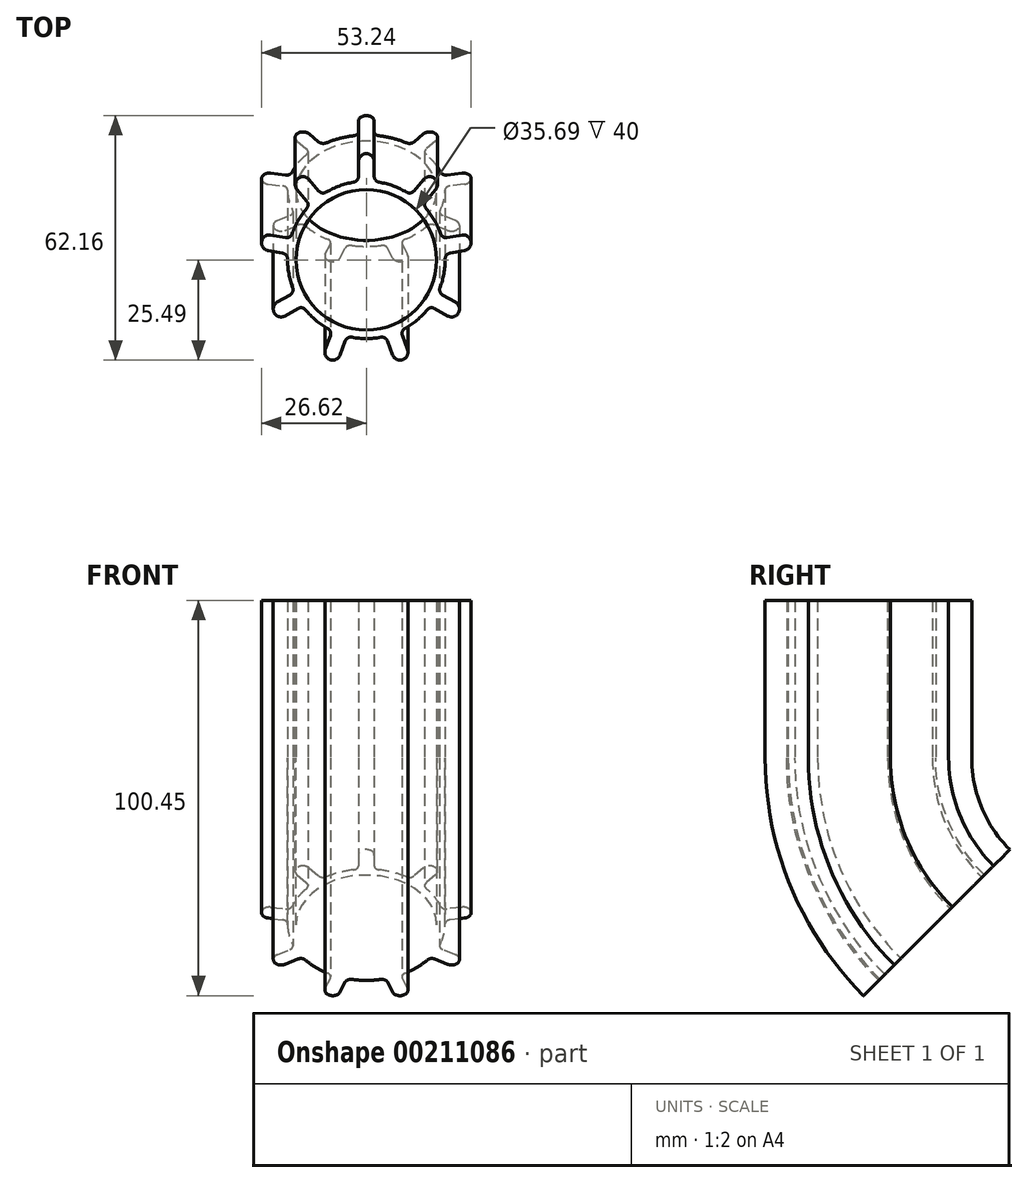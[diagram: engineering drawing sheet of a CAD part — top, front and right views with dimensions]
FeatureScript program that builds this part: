
annotation { "Feature Type Name" : "Feature", "Feature Type Description" : "" }
export const myFeature = defineFeature(function(context is Context, id is Id, definition is map)
    precondition{}
    {
        {
            var Q0;
            Q0=qCreatedBy(makeId("Top.planeOp"),FACE);
            var sketch = newSketch(context, id + "F0", { "sketchPlane" : qUnion([Q0])});
            skArc(sketch, "E0", {"start": v(-3.26, 19.73) * mm, "mid": v(-6.84, 18.8) * mm, "end": v(-10.2, 17.2) * mm});
            skArc(sketch, "E1", {"start": v(2, 25) * mm, "mid": v(0, 27) * mm, "end": v(-2, 25) * mm});
            skLineSegment(sketch, "E2", {"start": v(-2, 25) * mm, "end": v(-2, 21.21) * mm});
            skLineSegment(sketch, "E3", {"start": v(2, 25) * mm, "end": v(2, 21.21) * mm});
            skPoint(sketch, "E4.visualSharp", {"position": v(-2, 19.9) * mm});
            skArc(sketch, "E4.filletArc", {"start": v(-3.26, 19.73) * mm, "mid": v(-2.36, 20.24) * mm, "end": v(-2, 21.21) * mm});
            skPoint(sketch, "E5.visualSharp", {"position": v(2, 19.9) * mm});
            skArc(sketch, "E5.filletArc", {"start": v(2, 21.21) * mm, "mid": v(2.36, 20.24) * mm, "end": v(3.26, 19.73) * mm});
            skArc(sketch, "E6.1.0", {"start": v(-15.18, 13.02) * mm, "mid": v(-14.82, 14) * mm, "end": v(-15.17, 14.96) * mm});
            skLineSegment(sketch, "E6.1.1", {"start": v(-17.6, 17.87) * mm, "end": v(-15.17, 14.96) * mm});
            skArc(sketch, "E6.1.2", {"start": v(-14.54, 20.44) * mm, "mid": v(-17.36, 20.68) * mm, "end": v(-17.6, 17.87) * mm});
            skLineSegment(sketch, "E6.1.3", {"start": v(-14.54, 20.44) * mm, "end": v(-12.1, 17.54) * mm});
            skArc(sketch, "E6.1.4", {"start": v(-12.1, 17.54) * mm, "mid": v(-11.2, 17.02) * mm, "end": v(-10.2, 17.2) * mm});
            skArc(sketch, "E6.2.0", {"start": v(-20, 0.22) * mm, "mid": v(-20.34, 1.2) * mm, "end": v(-21.24, 1.71) * mm});
            skLineSegment(sketch, "E6.2.1", {"start": v(-24.97, 2.37) * mm, "end": v(-21.24, 1.71) * mm});
            skArc(sketch, "E6.2.2", {"start": v(-24.27, 6.31) * mm, "mid": v(-26.59, 4.69) * mm, "end": v(-24.97, 2.37) * mm});
            skLineSegment(sketch, "E6.2.3", {"start": v(-24.27, 6.31) * mm, "end": v(-20.54, 5.65) * mm});
            skArc(sketch, "E6.2.4", {"start": v(-20.54, 5.65) * mm, "mid": v(-19.53, 5.84) * mm, "end": v(-18.87, 6.63) * mm});
            skArc(sketch, "E6.3.0", {"start": v(-15.46, -12.69) * mm, "mid": v(-16.35, -12.16) * mm, "end": v(-17.37, -12.34) * mm});
            skLineSegment(sketch, "E6.3.1", {"start": v(-20.65, -14.23) * mm, "end": v(-17.37, -12.34) * mm});
            skArc(sketch, "E6.3.2", {"start": v(-22.65, -10.77) * mm, "mid": v(-23.38, -13.5) * mm, "end": v(-20.65, -14.23) * mm});
            skLineSegment(sketch, "E6.3.3", {"start": v(-22.65, -10.77) * mm, "end": v(-19.37, -8.87) * mm});
            skArc(sketch, "E6.3.4", {"start": v(-19.37, -8.87) * mm, "mid": v(-18.7, -8.08) * mm, "end": v(-18.72, -7.05) * mm});
            skArc(sketch, "E6.4.0", {"start": v(-3.69, -19.66) * mm, "mid": v(-4.7, -19.83) * mm, "end": v(-5.38, -20.62) * mm});
            skLineSegment(sketch, "E6.4.1", {"start": v(-6.67, -24.18) * mm, "end": v(-5.38, -20.62) * mm});
            skArc(sketch, "E6.4.2", {"start": v(-10.43, -22.8) * mm, "mid": v(-9.23, -25.37) * mm, "end": v(-6.67, -24.18) * mm});
            skLineSegment(sketch, "E6.4.3", {"start": v(-10.43, -22.8) * mm, "end": v(-9.13, -19.25) * mm});
            skArc(sketch, "E6.4.4", {"start": v(-9.13, -19.25) * mm, "mid": v(-9.14, -18.22) * mm, "end": v(-9.8, -17.43) * mm});
            skArc(sketch, "E6.5.0", {"start": v(9.8, -17.43) * mm, "mid": v(9.14, -18.22) * mm, "end": v(9.13, -19.25) * mm});
            skLineSegment(sketch, "E6.5.1", {"start": v(10.43, -22.8) * mm, "end": v(9.13, -19.25) * mm});
            skArc(sketch, "E6.5.2", {"start": v(6.67, -24.18) * mm, "mid": v(9.23, -25.37) * mm, "end": v(10.43, -22.8) * mm});
            skLineSegment(sketch, "E6.5.3", {"start": v(6.67, -24.18) * mm, "end": v(5.38, -20.62) * mm});
            skArc(sketch, "E6.5.4", {"start": v(5.38, -20.62) * mm, "mid": v(4.7, -19.83) * mm, "end": v(3.69, -19.66) * mm});
            skArc(sketch, "E6.6.0", {"start": v(18.72, -7.05) * mm, "mid": v(18.7, -8.08) * mm, "end": v(19.37, -8.87) * mm});
            skLineSegment(sketch, "E6.6.1", {"start": v(22.65, -10.77) * mm, "end": v(19.37, -8.87) * mm});
            skArc(sketch, "E6.6.2", {"start": v(20.65, -14.23) * mm, "mid": v(23.38, -13.5) * mm, "end": v(22.65, -10.77) * mm});
            skLineSegment(sketch, "E6.6.3", {"start": v(20.65, -14.23) * mm, "end": v(17.37, -12.34) * mm});
            skArc(sketch, "E6.6.4", {"start": v(17.37, -12.34) * mm, "mid": v(16.35, -12.16) * mm, "end": v(15.46, -12.69) * mm});
            skArc(sketch, "E6.7.0", {"start": v(18.87, 6.63) * mm, "mid": v(19.53, 5.84) * mm, "end": v(20.54, 5.65) * mm});
            skLineSegment(sketch, "E6.7.1", {"start": v(24.27, 6.31) * mm, "end": v(20.54, 5.65) * mm});
            skArc(sketch, "E6.7.2", {"start": v(24.97, 2.37) * mm, "mid": v(26.59, 4.69) * mm, "end": v(24.27, 6.31) * mm});
            skLineSegment(sketch, "E6.7.3", {"start": v(24.97, 2.37) * mm, "end": v(21.24, 1.71) * mm});
            skArc(sketch, "E6.7.4", {"start": v(21.24, 1.71) * mm, "mid": v(20.34, 1.2) * mm, "end": v(20, 0.22) * mm});
            skArc(sketch, "E6.8.0", {"start": v(10.2, 17.2) * mm, "mid": v(11.2, 17.02) * mm, "end": v(12.1, 17.54) * mm});
            skLineSegment(sketch, "E6.8.1", {"start": v(14.54, 20.44) * mm, "end": v(12.1, 17.54) * mm});
            skArc(sketch, "E6.8.2", {"start": v(17.6, 17.87) * mm, "mid": v(17.36, 20.68) * mm, "end": v(14.54, 20.44) * mm});
            skLineSegment(sketch, "E6.8.3", {"start": v(17.6, 17.87) * mm, "end": v(15.17, 14.96) * mm});
            skArc(sketch, "E6.8.4", {"start": v(15.17, 14.96) * mm, "mid": v(14.82, 14) * mm, "end": v(15.18, 13.02) * mm});
            skArc(sketch, "E7.trimOffspring", {"start": v(-20, 0.22) * mm, "mid": v(-19.7, -3.47) * mm, "end": v(-18.72, -7.05) * mm});
            skArc(sketch, "E8.trimOffspring", {"start": v(-15.18, 13.02) * mm, "mid": v(-17.32, 10) * mm, "end": v(-18.87, 6.63) * mm});
            skArc(sketch, "E9.trimOffspring", {"start": v(10.2, 17.2) * mm, "mid": v(6.84, 18.8) * mm, "end": v(3.26, 19.73) * mm});
            skPoint(sketch, "E10.center.orphan", {"position": v(0, -25) * mm});
            skArc(sketch, "E11.trimOffspring", {"start": v(-3.69, -19.66) * mm, "mid": v(0, -20) * mm, "end": v(3.69, -19.66) * mm});
            skArc(sketch, "E12.trimOffspring", {"start": v(-15.46, -12.69) * mm, "mid": v(-12.86, -15.32) * mm, "end": v(-9.8, -17.43) * mm});
            skArc(sketch, "E13.trimOffspring", {"start": v(9.8, -17.43) * mm, "mid": v(12.86, -15.32) * mm, "end": v(15.46, -12.69) * mm});
            skArc(sketch, "E14.trimOffspring", {"start": v(18.72, -7.05) * mm, "mid": v(19.7, -3.47) * mm, "end": v(20, 0.22) * mm});
            skArc(sketch, "E15.trimOffspring", {"start": v(18.87, 6.63) * mm, "mid": v(17.32, 10) * mm, "end": v(15.18, 13.02) * mm});
            skCircle(sketch, "E16", {"center": v(0, 0) * mm, "radius": 17.84 * mm});
            skSolve(sketch);
        }
        {
            var Q0;
            Q0=qCreatedBy(makeId("Right.planeOp"),FACE);
            var sketch = newSketch(context, id + "F1", { "sketchPlane" : qUnion([Q0])});
            skLineSegment(sketch, "E17", {"start": v(0, 0) * mm, "end": v(0, -40) * mm});
            skPoint(sketch, "E18.visualSharp", {"position": v(0, -100) * mm});
            skArc(sketch, "E18.filletArc", {"start": v(0, -40) * mm, "mid": v(4.57, -62.96) * mm, "end": v(17.57, -82.43) * mm});
            skLineSegment(sketch, "E19", {"start": v(0, -100) * mm, "end": v(17.57, -82.43) * mm});
            skLineSegment(sketch, "E20", {"start": v(0, -100) * mm, "end": v(0, -40) * mm, "construction": true});
            skPoint(sketch, "E21.end.orphan", {"position": v(100, -100) * mm});
            skSolve(sketch);
        }
        {
            var Q0;
            Q0=makeQuery(id+"F0.imprint","IMPRINT",FACE,{"disambiguationData":[TD([[makeQuery(id+"F0.imprint","IMPRINT",EDGE,{"derivedFrom":sQuery(id+"F0.wireOp",EDGE,"E0")}),1.0]])]});
            var Q1;
            Q1=sQuery(id+"F1.wireOp",EDGE,"E17");
            var Q2;
            Q2=sQuery(id+"F1.wireOp",EDGE,"E18.filletArc");
            var Q3;
            Q3=sQuery(id+"F1.wireOp",EDGE,"E21");
            sweep(context, id + "F2", {"profiles" : qUnion([Q0]), "path" : qUnion([Q1, Q2, Q3])});
        }
    });
